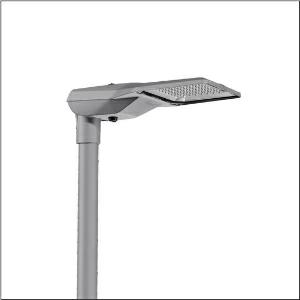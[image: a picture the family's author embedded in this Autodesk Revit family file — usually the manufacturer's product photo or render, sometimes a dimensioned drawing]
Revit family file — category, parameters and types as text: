
# Revit family: streetlight_sl_21_iq_midi___st1_0a_5xe3d21y08mb_afa7
name_source: partatom
category: Lighting Fixtures
units: mm (PartAtom-declared; Revit-internal decimal feet)

## family parameters
Cut with Voids When Loaded = No
Host = Face
Light Source = No
Part Type = Normal
Room Calculation Point = No
Round Connector Dimension = Use Diameter
Shared = No

## types (1)
- --- (1 x LED, 14710 lm, 129.3 W, 2200K)
    Apparent Load = 129 VA
    CIE Flux Codes = 37 72 97 100 100
    Color Rendering = 70
    Color Temperature = 2200K
    Default Elevation = 1800 mm
    Description = Streetlight SL 21 iQ midi, mast luminaire, primary light control with lens, of PMMA, primary optical cover: cover, of toughened safety glass, transparent, light distribution: ST1.0a, light emission: direct distribution, primary light characteristic: asymmetric, installation type: post-top, side-entry, LED, High Power LED, rated luminous flux: 14.710lm, luminous efficacy: 114lm/W, light colour: 722, colour temperature: 2200K, control: presetting dimming logarithmic, Street-Remote, Auto-Match, Temp-Guard, Lumen-Switch, Night-Set, Smart-Wire, Light-Fading, Desk-Remote (wireless, voltage-free reading and setting of iQ features in the workshop via application-optimized NFC function/RFID function), optimised constant luminous flux control (CLO 2.0), mains connection: 230..240V, AC, 50/60Hz, start of lifetime: 129W, end of service life: 142W, reduction: 56W, luminaire housing, of diecast aluminium, powder-coated, Siteco® metallic grey (DB 702S), corrosivity category C5 mid according to DIN EN ISO 12944, please order mast flange separately, inclination adjustable: 0°, 5°, 10°, 15°, sealing non-destructively replaceable, multi-level sealing system, length: 644mm, width: 335mm, height: 110mm, mast flange for spigot size: 42mm (side-entry): 5XC10008XM4, 60/48mm (side-entry/post-top): 5XC10108XM2, 76/60mm (side-entry/post-top): 5XC10108XM1, Smart Interface below and above, protection rating (complete): IP66, insulation class (complete): insulation class II (safety insulation), certification: CE, ENEC, ENEC+, VDE, impact resistance: IK09, permissible operating ambient temperature for outdoor applications: -40..+50°C, standard-compliant lighting for roads and squares, packaging unit: 1 piece

Light Distribution: ST1.0a
    Height = 111 mm
    Lamp = 1 x LED
    Lamp Light Flux = 14710 lm
    Lamp Power = 129.3 W
    Lamp count = 1
    Length = 644 mm
    Luminous efficacy = 114 lm/W
    Manufacturer = Siteco
    ModVariant = No
    Model = 5XE3D21Y08MB
    Number of Poles = 1
    OnlyDefault = Yes
    Power Factor = 1
    Product Name = Streetlight SL 21 iQ midi | ST1.0a
    Product group = mast luminaire | pylon top
    ProductGroupID = 6100
    Protection Class = Protection class II
    Protection Degree = IP 66
    RLX_Detail_Level = 1
    RLX_Emergency_Light_Flux = 0 lm
    RLX_Emergency_Type = 0
    RLX_Emergency_Type_DB = No
    RlxData = <blob elided: 90665 chars, md5=16ac248e>
    Socket = socket
    Standby Power = 0 W
    System Light Flux = 14710 lm
    System Power = 129 W
    Type Comments = factory setting: luminous flux: 100 % | dim-lin: 254 | 672 mA
    Type Image = l_1004304.jpg
    URL = http://relux.com
    VarID = @adj_044645
    Voltage = 0 V
    Weight = 0.00 kg
    Width = 336 mm

## geometry (parser evidence)
native form markers: Blend x4, Sweep x10
no freeform markers — native parametric forms only
